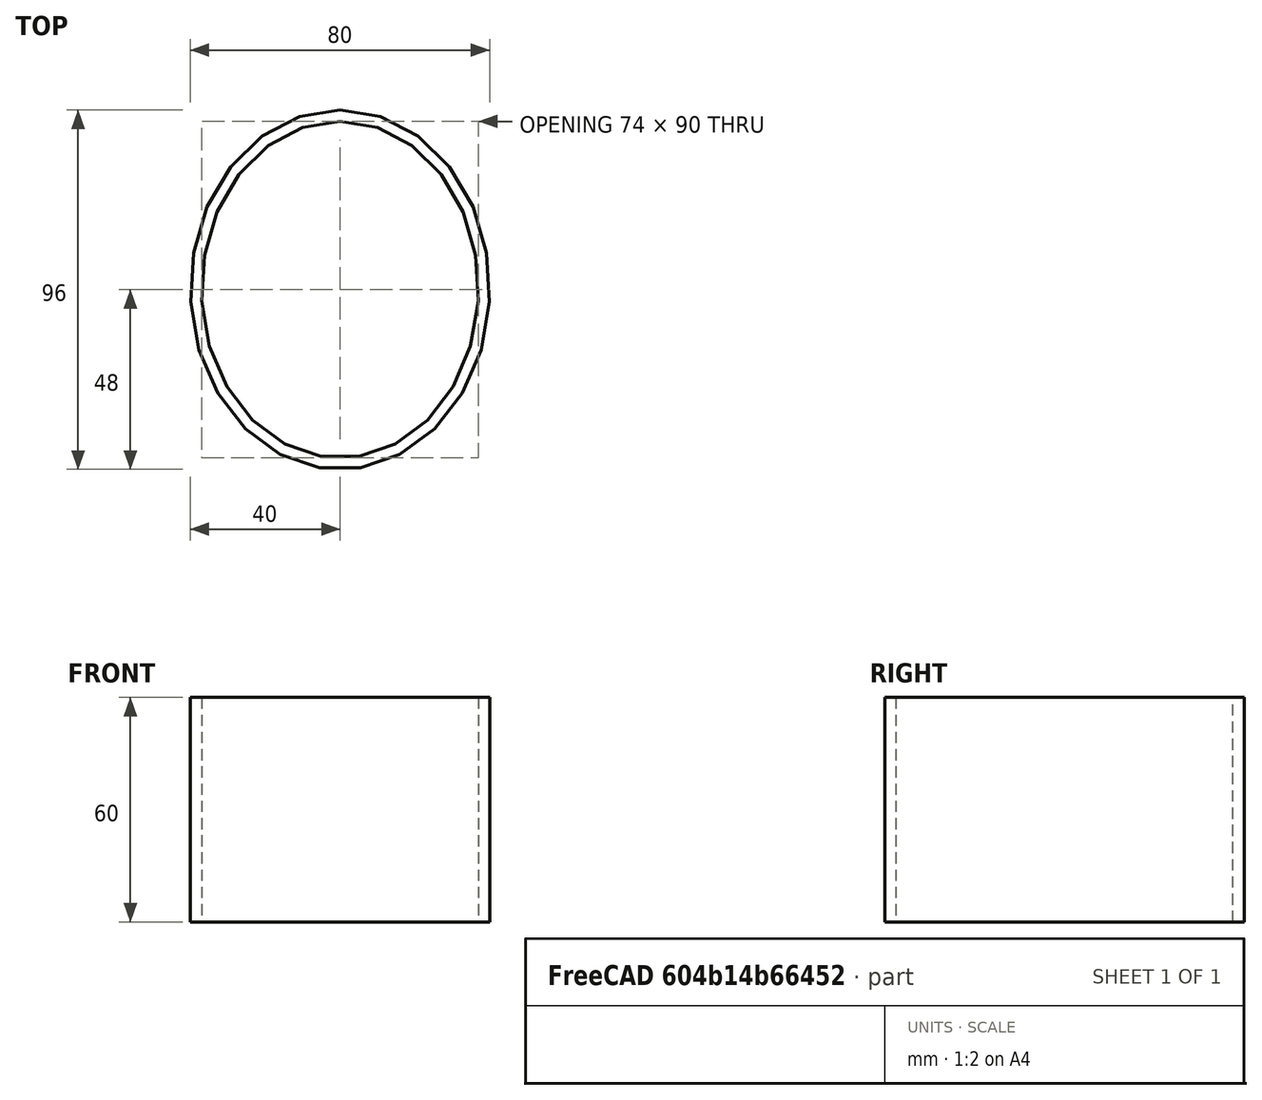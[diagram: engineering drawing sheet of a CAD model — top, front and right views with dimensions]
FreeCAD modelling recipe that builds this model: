
FCSTD DOCUMENT  (FreeCAD 0.19R24291 (Git))
Label: Base-Lidar
License: All rights reserved
LicenseURL: http://en.wikipedia.org/wiki/All_rights_reserved
objects: Sketcher::SketchObject×1, PartDesign::Pad×1, PartDesign::Body×1
note: 4 computed .brp shape members not serialized (recipe doc carries the construction recipe); baked Part::Feature solids carry a one-line shape summary decoded from their .brp

FEATURE [Sketcher::SketchObject] Sketch
  FullyConstrained = true
  MapMode = 5
  Support = -> [XY_Plane]
  sketch-geometry (21):
    g0: LineSegment StartX=-50 StartY=-50 StartZ=0 EndX=50 EndY=-50 EndZ=0
    g1: LineSegment StartX=50 StartY=-50 StartZ=0 EndX=50 EndY=50 EndZ=0
    g2: LineSegment StartX=50 StartY=50 StartZ=0 EndX=-50 EndY=50 EndZ=0
    g3: LineSegment StartX=-50 StartY=50 StartZ=0 EndX=-50 EndY=-50 EndZ=0
    g4: LineSegment StartX=-50 StartY=-50 StartZ=0 EndX=50 EndY=50 EndZ=0
    g5: LineSegment StartX=-50 StartY=50 StartZ=0 EndX=50 EndY=-50 EndZ=0
    g6: LineSegment StartX=-40 StartY=50 StartZ=0 EndX=-40 EndY=-50 EndZ=0
    g7: LineSegment StartX=40 StartY=50 StartZ=0 EndX=40 EndY=-50 EndZ=0
    g8: GeomPoint X=-40 Y=0 Z=0
    g9: Ellipse CenterX=0 CenterY=0 CenterZ=0 NormalX=0 NormalY=0 NormalZ=1 MajorRadius=48 MinorRadius=40 AngleXU=1.5708
    g10: LineSegment StartX=0 StartY=48 StartZ=0 EndX=0 EndY=-48 EndZ=0
    g11: LineSegment StartX=-40 StartY=1e-16 StartZ=0 EndX=40 EndY=-1e-16 EndZ=0
    g12: GeomPoint X=2.9e-15 Y=26.533 Z=0
    g13: GeomPoint X=1e-16 Y=-26.533 Z=0
    g14: GeomPoint X=-37 Y=1e-16 Z=0
    g15: Ellipse CenterX=0 CenterY=0 CenterZ=0 NormalX=0 NormalY=0 NormalZ=1 MajorRadius=45 MinorRadius=37 AngleXU=1.5708
    g16: LineSegment StartX=0 StartY=45 StartZ=0 EndX=0 EndY=-45 EndZ=0
    g17: LineSegment StartX=-37 StartY=1e-16 StartZ=0 EndX=37 EndY=-1e-16 EndZ=0
    g18: GeomPoint X=2.8e-15 Y=25.6125 Z=0
    g19: GeomPoint X=1e-16 Y=-25.6125 Z=0
    g20: GeomPoint X=0 Y=48 Z=0
  constraints (40):
    c: Coincident(g0,g1)
    c: Coincident(g1,g2)
    c: Coincident(g2,g3)
    c: Coincident(g3,g0)
    c: Horizontal(g0)
    c: Horizontal(g2)
    c: Vertical(g1)
    c: Vertical(g3)
    c: Coincident(g4,g0)
    c: Coincident(g4,g1)
    c: Coincident(g5,g2)
    c: Coincident(g5,g0)
    c: PointOnObject(g-1,g5)
    c: PointOnObject(g-1,g4)
    c: DistanceY(g1,g1) = 100
    c: Equal(g1,g2)
    c: PointOnObject(g6,g2)
    c: PointOnObject(g6,g0)
    c: Vertical(g6)
    c: PointOnObject(g7,g2)
    c: PointOnObject(g7,g0)
    c: Vertical(g7)
    c: DistanceX(g0,g6) = 10
    c: DistanceX(g7,g0) = 10
    c: PointOnObject(g8,g6)
    c: PointOnObject(g8,g-1)
    c: InternalAlignment(g10-g13 -> g9) x4
    c: Coincident(g9,g-1)
    c: PointOnObject(g8,g9)
    c: PointOnObject(g10,g-2)
    c: PointOnObject(g14,g11)
    c: DistanceX(g8,g14) = 3
    c: InternalAlignment(g16-g19 -> g15) x4
    c: Coincident(g15,g9)
    c: PointOnObject(g14,g15)
    c: Vertical(g16,g10)
    c: PointOnObject(g20,g-2)
    c: PointOnObject(g20,g9)
    c: DistanceY(g16,g10) = 3
    c: DistanceY(g10,g6) = 2
FEATURE [PartDesign::Pad] Pad  label="Base"
  Direction = (1,1,1)
  Length = 60
  Length2 = 100
  Profile = -> Sketch
  Type = 0
FEATURE [PartDesign::Body] Body
  Group = -> [Sketch,Pad]
  Origin = -> Origin
  Tip = -> Pad
